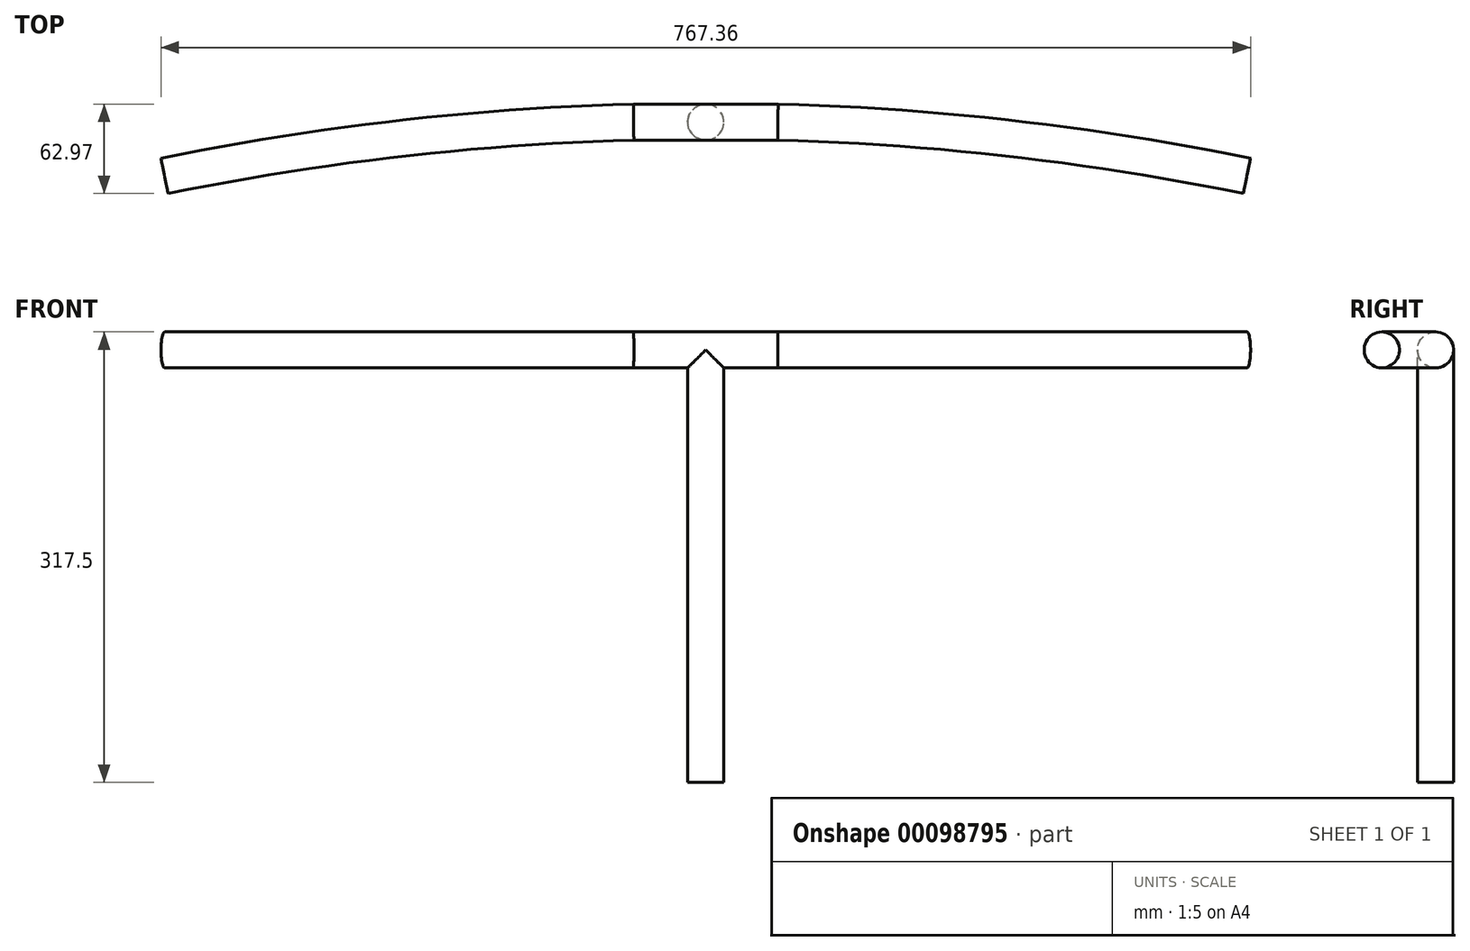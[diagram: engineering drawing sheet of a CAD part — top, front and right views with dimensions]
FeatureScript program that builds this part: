
annotation { "Feature Type Name" : "Feature", "Feature Type Description" : "" }
export const myFeature = defineFeature(function(context is Context, id is Id, definition is map)
    precondition{}
    {
        {
            var Q0;
            Q0=qCreatedBy(makeId("Top.planeOp"),FACE);
            var sketch = newSketch(context, id + "F0", { "sketchPlane" : qUnion([Q0])});
            skArc(sketch, "E0", {"start": v(381, -38.49) * mm, "mid": v(216.73, -12.37) * mm, "end": v(50.8, -0.68) * mm});
            skLineSegment(sketch, "E1", {"start": v(381, 42.31) * mm, "end": v(381, -69.3) * mm});
            skLineSegment(sketch, "E2", {"start": v(-50.8, 11.5) * mm, "end": v(-50.8, -3.43) * mm});
            skLineSegment(sketch, "E3", {"start": v(50.8, 12.02) * mm, "end": v(50.8, -28.58) * mm});
            skPoint(sketch, "E4", {"position": v(-50.8, -0.68) * mm});
            skLineSegment(sketch, "E5", {"start": v(-50.8, -0.68) * mm, "end": v(0, -0.68) * mm});
            skArc(sketch, "E6", {"start": v(-50.8, -0.68) * mm, "mid": v(-216.73, -12.37) * mm, "end": v(-381, -38.49) * mm});
            skLineSegment(sketch, "E7", {"start": v(-50.8, -3.43) * mm, "end": v(-50.8, -29.1) * mm});
            skLineSegment(sketch, "E8", {"start": v(0, -0.68) * mm, "end": v(50.8, -0.68) * mm});
            skSolve(sketch);
        }
        {
            var Q0;
            Q0=qCreatedBy(makeId("Right.planeOp"),FACE);
            var sketch = newSketch(context, id + "F1", { "sketchPlane" : qUnion([Q0])});
            skCircle(sketch, "E9", {"center": v(0, 0) * mm, "radius": 12.7 * mm});
            skSolve(sketch);
        }
        {
            var Q0;
            Q0=makeQuery(id+"F1.imprint","IMPRINT",FACE,{"disambiguationData":[TD([[makeQuery(id+"F1.imprint","IMPRINT",EDGE,{"derivedFrom":sQuery(id+"F1.wireOp",EDGE,"E9")}),1.0]])]});
            var Q1;
            Q1=sQuery(id+"F0.wireOp",EDGE,"E8");
            var Q2;
            Q2=sQuery(id+"F0.wireOp",EDGE,"E0");
            sweep(context, id + "F2", {"profiles" : qUnion([Q0]), "path" : qUnion([Q1, Q2])});
        }
        {
            var Q0;
            Q0=makeQuery(id+"F2.opSweep","CAP_FACE",FACE,{"disambiguationData":[OSD([sQuery(id+"F0.wireOp",VERTEX,"E8.start"),sQuery(id+"F1.wireOp",EDGE,"E9")])],"isStart":true});
            var Q1;
            Q1=sQuery(id+"F0.wireOp",EDGE,"E5");
            var Q2;
            Q2=sQuery(id+"F0.wireOp",EDGE,"E6");
            sweep(context, id + "F3", {"operationType" : NewBodyOperationType.ADD, "profiles" : qUnion([Q0]), "path" : qUnion([Q1, Q2])});
        }
        {
            var Q0;
            Q0=qCreatedBy(makeId("Top.planeOp"),FACE);
            var sketch = newSketch(context, id + "F4", { "sketchPlane" : qUnion([Q0])});
            skCircle(sketch, "E10", {"center": v(0, 0) * mm, "radius": 12.7 * mm});
            skSolve(sketch);
        }
        {
            var Q0;
            Q0 = qSketchRegion(id + "F4", true);
            extrude(context, id + "F5", {"entities" : qUnion([Q0]), "operationType" : NewBodyOperationType.ADD, "oppositeDirection" : true, "depth" : 304.8 * mm});
        }
    });
